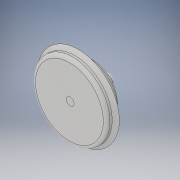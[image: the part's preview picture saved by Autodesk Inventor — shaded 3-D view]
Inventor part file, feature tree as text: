
AUTODESK INVENTOR PART (.ipt)
format: ipt  version: 2017 (Build 210142000, 142)  size: 172,544 bytes
history: native  units: in
note: dims shown in document units (in); Inventor stores cm internally (conversion verified against a paired STEP export)
features: revolve x1, fillet x1, sketch x1
ambient origin geometry x8: Origin, YZ Plane, XZ Plane, XY Plane, X Axis, Y Axis, Z Axis, Center Point
bodies: Solid1 (feature_tree)
feature tree (3):
  revolve  "Revolution1"  Angle=90.0deg
  fillet  "Fillet1"  Radius=0.05in
  sketch  "Sketch1"  dims[d0=0.5in d1=90.0deg d2=0.05in]
